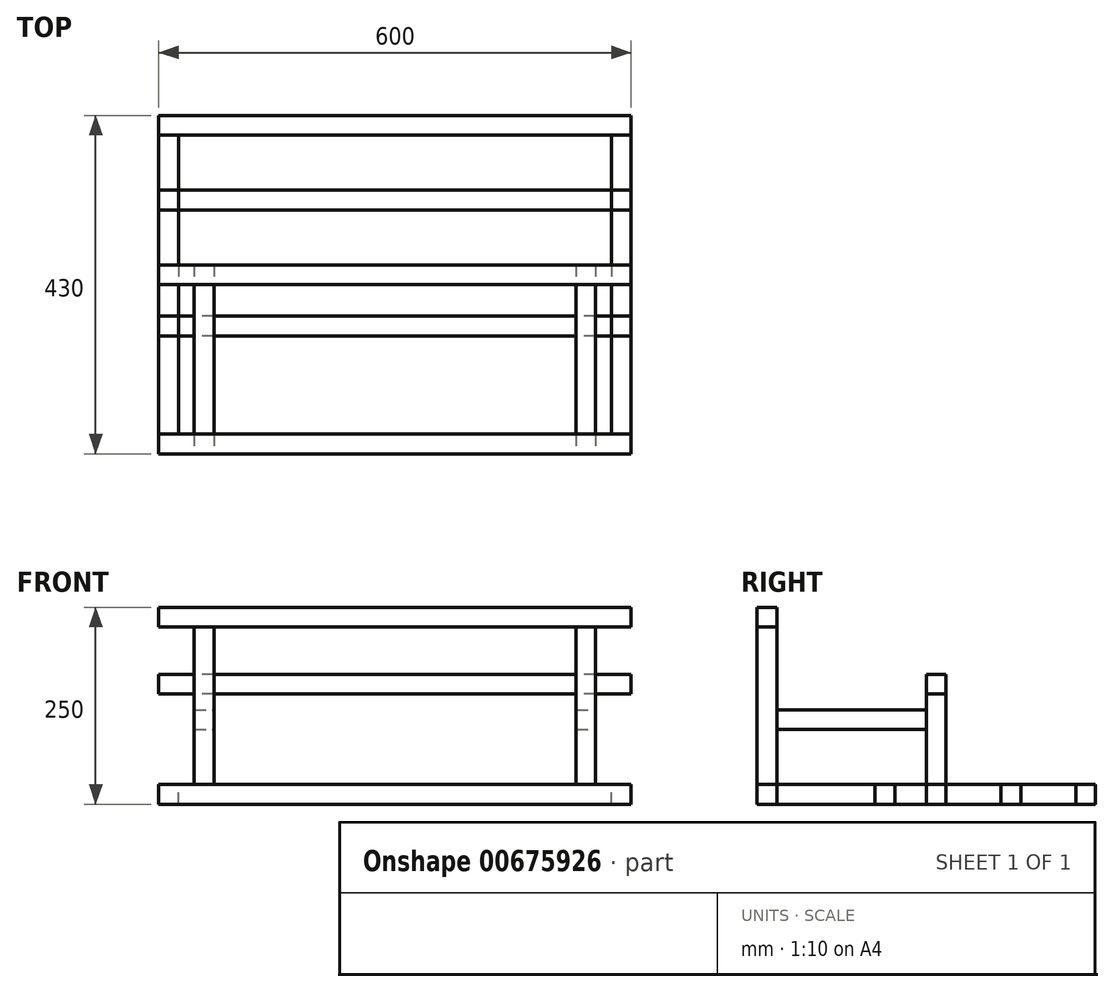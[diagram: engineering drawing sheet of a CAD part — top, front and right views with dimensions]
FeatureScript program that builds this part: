
annotation { "Feature Type Name" : "Feature", "Feature Type Description" : "" }
export const myFeature = defineFeature(function(context is Context, id is Id, definition is map)
    precondition{}
    {
        {
            var Q0;
            Q0=qCreatedBy(makeId("Right.planeOp"),FACE);
            var sketch = newSketch(context, id + "F0", { "sketchPlane" : qUnion([Q0])});
            skLineSegment(sketch, "E0.bottom", {"start": v(-12.5, 12.5) * mm, "end": v(12.5, 12.5) * mm});
            skLineSegment(sketch, "E0.top", {"start": v(-12.5, -12.5) * mm, "end": v(12.5, -12.5) * mm});
            skLineSegment(sketch, "E0.left", {"start": v(-12.5, 12.5) * mm, "end": v(-12.5, -12.5) * mm});
            skLineSegment(sketch, "E0.right", {"start": v(12.5, 12.5) * mm, "end": v(12.5, -12.5) * mm});
            skPoint(sketch, "E0.middle", {"position": v(0, 0) * mm});
            skLineSegment(sketch, "E1.bottom", {"start": v(392.5, -12.5) * mm, "end": v(417.5, -12.5) * mm});
            skLineSegment(sketch, "E1.top", {"start": v(392.5, 12.5) * mm, "end": v(417.5, 12.5) * mm});
            skLineSegment(sketch, "E1.left", {"start": v(392.5, -12.5) * mm, "end": v(392.5, 12.5) * mm});
            skLineSegment(sketch, "E1.right", {"start": v(417.5, -12.5) * mm, "end": v(417.5, 12.5) * mm});
            skPoint(sketch, "E1.middle", {"position": v(405, 0) * mm});
            skLineSegment(sketch, "E2.bottom", {"start": v(137.5, -12.5) * mm, "end": v(162.5, -12.5) * mm});
            skLineSegment(sketch, "E2.top", {"start": v(137.5, 12.5) * mm, "end": v(162.5, 12.5) * mm});
            skLineSegment(sketch, "E2.left", {"start": v(137.5, -12.5) * mm, "end": v(137.5, 12.5) * mm});
            skLineSegment(sketch, "E2.right", {"start": v(162.5, -12.5) * mm, "end": v(162.5, 12.5) * mm});
            skPoint(sketch, "E2.middle", {"position": v(150, 0) * mm});
            skLineSegment(sketch, "E3.bottom", {"start": v(202.5, -12.5) * mm, "end": v(227.5, -12.5) * mm});
            skLineSegment(sketch, "E3.top", {"start": v(202.5, 12.5) * mm, "end": v(227.5, 12.5) * mm});
            skLineSegment(sketch, "E3.left", {"start": v(202.5, -12.5) * mm, "end": v(202.5, 12.5) * mm});
            skLineSegment(sketch, "E3.right", {"start": v(227.5, -12.5) * mm, "end": v(227.5, 12.5) * mm});
            skPoint(sketch, "E3.middle", {"position": v(215, 0) * mm});
            skLineSegment(sketch, "E4.bottom", {"start": v(-12.5, 212.5) * mm, "end": v(12.5, 212.5) * mm});
            skLineSegment(sketch, "E4.top", {"start": v(-12.5, 237.5) * mm, "end": v(12.5, 237.5) * mm});
            skLineSegment(sketch, "E4.left", {"start": v(-12.5, 212.5) * mm, "end": v(-12.5, 237.5) * mm});
            skLineSegment(sketch, "E4.right", {"start": v(12.5, 212.5) * mm, "end": v(12.5, 237.5) * mm});
            skPoint(sketch, "E4.middle", {"position": v(0, 225) * mm});
            skLineSegment(sketch, "E5.bottom", {"start": v(202.5, 127.5) * mm, "end": v(227.5, 127.5) * mm});
            skLineSegment(sketch, "E5.top", {"start": v(202.5, 152.5) * mm, "end": v(227.5, 152.5) * mm});
            skLineSegment(sketch, "E5.left", {"start": v(202.5, 127.5) * mm, "end": v(202.5, 152.5) * mm});
            skLineSegment(sketch, "E5.right", {"start": v(227.5, 127.5) * mm, "end": v(227.5, 152.5) * mm});
            skPoint(sketch, "E5.middle", {"position": v(215, 140) * mm});
            skLineSegment(sketch, "E6.bottom", {"start": v(297.5, -12.5) * mm, "end": v(322.5, -12.5) * mm});
            skLineSegment(sketch, "E6.top", {"start": v(297.5, 12.5) * mm, "end": v(322.5, 12.5) * mm});
            skLineSegment(sketch, "E6.left", {"start": v(297.5, -12.5) * mm, "end": v(297.5, 12.5) * mm});
            skLineSegment(sketch, "E6.right", {"start": v(322.5, -12.5) * mm, "end": v(322.5, 12.5) * mm});
            skPoint(sketch, "E6.middle", {"position": v(310, 0) * mm});
            skLineSegment(sketch, "E7", {"start": v(405, 0) * mm, "end": v(215, 0) * mm, "construction": true});
            skSolve(sketch);
        }
        {
            var Q0;
            Q0 = qSketchRegion(id + "F0", true);
            extrude(context, id + "F1", {"entities" : qUnion([Q0]), "depth" : 600 * mm, "offsetDistance" : 25 * mm});
        }
        {
            var Q0;
            Q0=makeQuery(id+"F1.opExtrude","SWEPT_FACE",FACE,{"disambiguationData":[OSD([sQuery(id+"F0.wireOp",EDGE,"E0.right")])]});
            var sketch = newSketch(context, id + "F2", { "sketchPlane" : qUnion([Q0])});
            skLineSegment(sketch, "E8.bottom", {"start": v(0, 12.5) * mm, "end": v(-25, 12.5) * mm});
            skLineSegment(sketch, "E8.top", {"start": v(0, -12.5) * mm, "end": v(-25, -12.5) * mm});
            skLineSegment(sketch, "E8.left", {"start": v(0, 12.5) * mm, "end": v(0, -12.5) * mm});
            skLineSegment(sketch, "E8.right", {"start": v(-25, 12.5) * mm, "end": v(-25, -12.5) * mm});
            skLineSegment(sketch, "E9.bottom", {"start": v(-600, 12.5) * mm, "end": v(-575, 12.5) * mm});
            skLineSegment(sketch, "E9.top", {"start": v(-600, -12.5) * mm, "end": v(-575, -12.5) * mm});
            skLineSegment(sketch, "E9.left", {"start": v(-600, 12.5) * mm, "end": v(-600, -12.5) * mm});
            skLineSegment(sketch, "E9.right", {"start": v(-575, 12.5) * mm, "end": v(-575, -12.5) * mm});
            skSolve(sketch);
        }
        {
            var Q0;
            Q0 = qSketchRegion(id + "F2", true);
            var Q1;
            Q1=makeQuery(id+"F1.opExtrude","SWEPT_BODY",BODY,{"disambiguationData":[OSD([sQuery(id+"F0.wireOp",EDGE,"E1.bottom"),sQuery(id+"F0.wireOp",EDGE,"E1.top"),sQuery(id+"F0.wireOp",EDGE,"E1.left"),sQuery(id+"F0.wireOp",EDGE,"E1.right")])]});
            extrude(context, id + "F3", {"entities" : qUnion([Q0]), "endBound" : BoundingType.UP_TO_BODY, "depth" : 378 * mm, "endBoundEntityBody" : qUnion([Q1]), "offsetDistance" : 25 * mm});
        }
        {
            var Q0;
            Q0=makeQuery(id+"F1.opExtrude","SWEPT_FACE",FACE,{"disambiguationData":[OSD([sQuery(id+"F0.wireOp",EDGE,"E3.top")])]});
            var sketch = newSketch(context, id + "F4", { "sketchPlane" : qUnion([Q0])});
            skLineSegment(sketch, "E10.bottom", {"start": v(555, 227.5) * mm, "end": v(530, 227.5) * mm});
            skLineSegment(sketch, "E10.top", {"start": v(555, 202.5) * mm, "end": v(530, 202.5) * mm});
            skLineSegment(sketch, "E10.left", {"start": v(555, 227.5) * mm, "end": v(555, 202.5) * mm});
            skLineSegment(sketch, "E10.right", {"start": v(530, 227.5) * mm, "end": v(530, 202.5) * mm});
            skLineSegment(sketch, "E11.bottom", {"start": v(45, 227.5) * mm, "end": v(70, 227.5) * mm});
            skLineSegment(sketch, "E11.top", {"start": v(45, 202.5) * mm, "end": v(70, 202.5) * mm});
            skLineSegment(sketch, "E11.left", {"start": v(45, 227.5) * mm, "end": v(45, 202.5) * mm});
            skLineSegment(sketch, "E11.right", {"start": v(70, 227.5) * mm, "end": v(70, 202.5) * mm});
            skLineSegment(sketch, "E12", {"start": v(555, 227.5) * mm, "end": v(575, 227.5) * mm, "construction": true});
            skLineSegment(sketch, "E13", {"start": v(45, 227.5) * mm, "end": v(25, 227.5) * mm, "construction": true});
            skSolve(sketch);
        }
        {
            var Q0;
            Q0 = qSketchRegion(id + "F4", true);
            extrude(context, id + "F5", {"entities" : qUnion([Q0]), "endBound" : BoundingType.UP_TO_NEXT, "depth" : 25 * mm, "offsetDistance" : 25 * mm});
        }
        {
            var Q0;
            Q0=makeQuery(id+"F1.opExtrude","SWEPT_FACE",FACE,{"disambiguationData":[OSD([sQuery(id+"F0.wireOp",EDGE,"E0.bottom")])]});
            var sketch = newSketch(context, id + "F6", { "sketchPlane" : qUnion([Q0])});
            skLineSegment(sketch, "E14.bottom", {"start": v(555, 12.5) * mm, "end": v(530, 12.5) * mm});
            skLineSegment(sketch, "E14.top", {"start": v(555, -12.5) * mm, "end": v(530, -12.5) * mm});
            skLineSegment(sketch, "E14.left", {"start": v(555, 12.5) * mm, "end": v(555, -12.5) * mm});
            skLineSegment(sketch, "E14.right", {"start": v(530, 12.5) * mm, "end": v(530, -12.5) * mm});
            skLineSegment(sketch, "E15.bottom", {"start": v(70, 12.5) * mm, "end": v(45, 12.5) * mm});
            skLineSegment(sketch, "E15.top", {"start": v(70, -12.5) * mm, "end": v(45, -12.5) * mm});
            skLineSegment(sketch, "E15.left", {"start": v(70, 12.5) * mm, "end": v(70, -12.5) * mm});
            skLineSegment(sketch, "E15.right", {"start": v(45, 12.5) * mm, "end": v(45, -12.5) * mm});
            skLineSegment(sketch, "E16", {"start": v(45, 12.5) * mm, "end": v(25, 12.5) * mm, "construction": true});
            skLineSegment(sketch, "E17", {"start": v(555, 12.5) * mm, "end": v(575, 12.5) * mm, "construction": true});
            skSolve(sketch);
        }
        {
            var Q0;
            Q0 = qSketchRegion(id + "F6", true);
            extrude(context, id + "F7", {"entities" : qUnion([Q0]), "endBound" : BoundingType.UP_TO_NEXT, "depth" : 25 * mm, "offsetDistance" : 25 * mm});
        }
        {
            var Q0;
            Q0=makeQuery(id+"F5.opExtrude","SWEPT_FACE",FACE,{"disambiguationData":[OSD([sQuery(id+"F4.wireOp",EDGE,"E11.top")])]});
            var sketch = newSketch(context, id + "F8", { "sketchPlane" : qUnion([Q0])});
            skLineSegment(sketch, "E18.bottom", {"start": v(45, 107.5) * mm, "end": v(70, 107.5) * mm});
            skLineSegment(sketch, "E18.top", {"start": v(45, 82.5) * mm, "end": v(70, 82.5) * mm});
            skLineSegment(sketch, "E18.left", {"start": v(45, 107.5) * mm, "end": v(45, 82.5) * mm});
            skLineSegment(sketch, "E18.right", {"start": v(70, 107.5) * mm, "end": v(70, 82.5) * mm});
            skLineSegment(sketch, "E19.bottom", {"start": v(530, 82.5) * mm, "end": v(555, 82.5) * mm});
            skLineSegment(sketch, "E19.top", {"start": v(530, 107.5) * mm, "end": v(555, 107.5) * mm});
            skLineSegment(sketch, "E19.left", {"start": v(530, 82.5) * mm, "end": v(530, 107.5) * mm});
            skLineSegment(sketch, "E19.right", {"start": v(555, 82.5) * mm, "end": v(555, 107.5) * mm});
            skLineSegment(sketch, "E20", {"start": v(45, 107.5) * mm, "end": v(45, 127.5) * mm, "construction": true});
            skLineSegment(sketch, "E21", {"start": v(530, 107.5) * mm, "end": v(530, 127.5) * mm, "construction": true});
            skSolve(sketch);
        }
        {
            var Q0;
            Q0 = qSketchRegion(id + "F8", true);
            extrude(context, id + "F9", {"entities" : qUnion([Q0]), "endBound" : BoundingType.UP_TO_NEXT, "depth" : 25 * mm, "offsetDistance" : 25 * mm});
        }
    });
